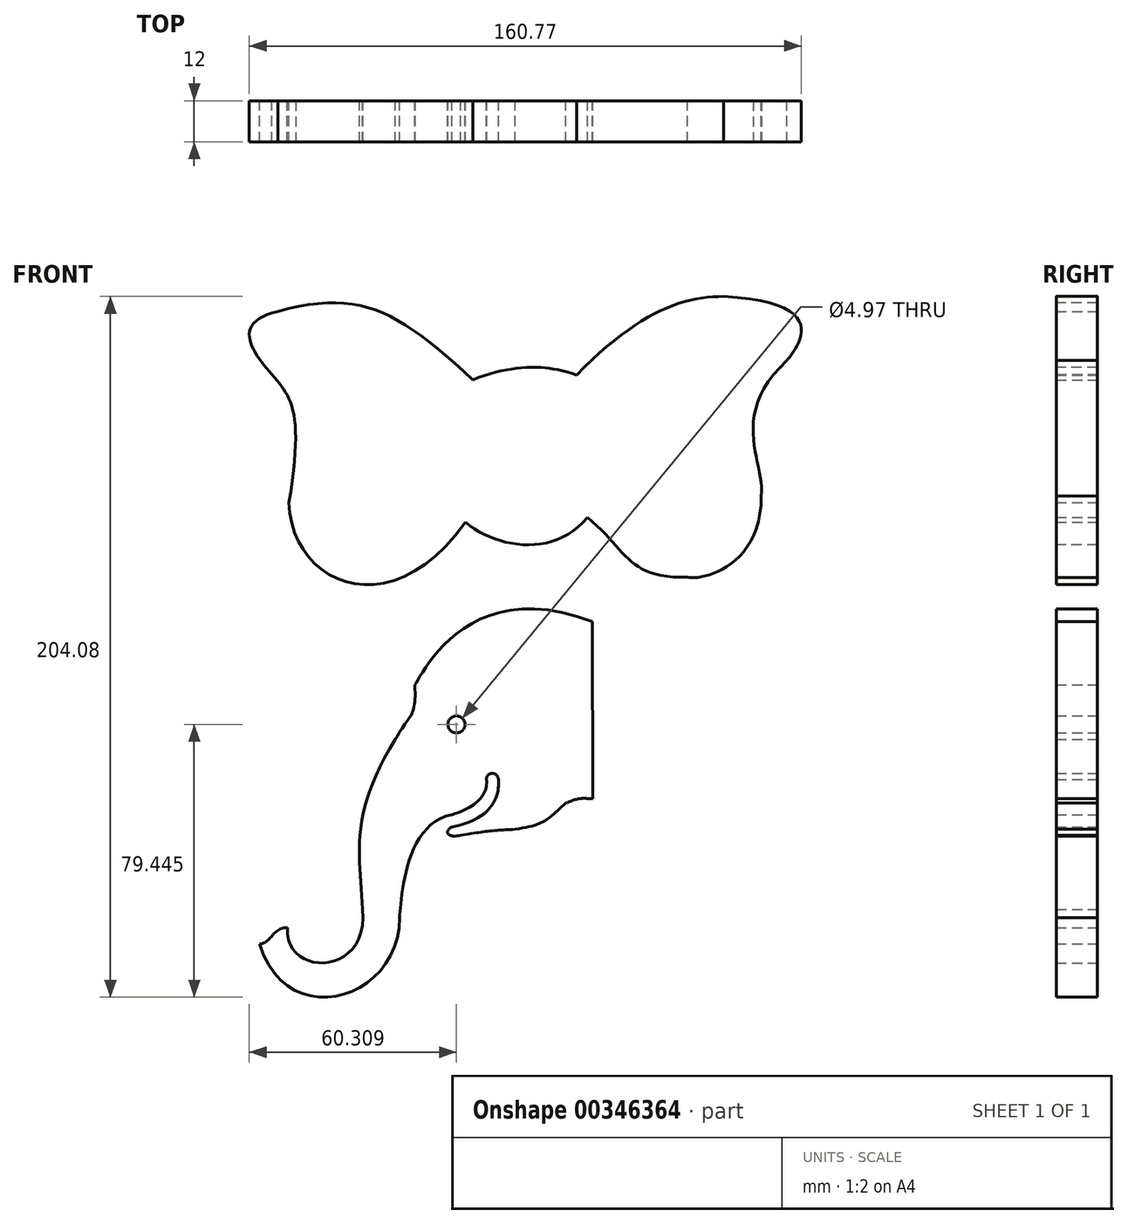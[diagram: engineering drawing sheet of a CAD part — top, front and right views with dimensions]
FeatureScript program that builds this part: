
annotation { "Feature Type Name" : "Feature", "Feature Type Description" : "" }
export const myFeature = defineFeature(function(context is Context, id is Id, definition is map)
    precondition{}
    {
        {
            var Q0;
            Q0=qCreatedBy(makeId("Front.planeOp"),FACE);
            var sketch = newSketch(context, id + "F0", { "sketchPlane" : qUnion([Q0])});
            skFitSpline(sketch, "E0", {"points": [v(-71.13, -54.1) * mm, v(-41, -52.71) * mm], "startDerivative": vector(38.1, 16.38) * mm, "endDerivative": vector(16.93, -7.18) * mm});
            skFitSpline(sketch, "E1", {"points": [v(-41, -52.71) * mm, v(1.84, -29.82) * mm], "startDerivative": vector(52.97, 54.2) * mm, "endDerivative": vector(35.72, -0.65) * mm});
            skFitSpline(sketch, "E2", {"points": [v(1.84, -29.82) * mm, v(20.3, -48.4) * mm], "startDerivative": vector(99.15, -5.13) * mm, "endDerivative": vector(-7.47, -9.38) * mm});
            skFitSpline(sketch, "E3", {"points": [v(20.3, -48.4) * mm, v(12.8, -87.94) * mm], "startDerivative": vector(-52.35, -49.57) * mm, "endDerivative": vector(-3.9, -29.42) * mm});
            skFitSpline(sketch, "E4", {"points": [v(12.8, -87.94) * mm, v(-8.74, -111.56) * mm], "startDerivative": vector(0.04, -63.12) * mm, "endDerivative": vector(-11.14, 3.4) * mm});
            skFitSpline(sketch, "E5", {"points": [v(-8.74, -111.56) * mm, v(-37.79, -94.18) * mm], "startDerivative": vector(-52.12, -1.48) * mm, "endDerivative": vector(-35.02, 28.89) * mm});
            skFitSpline(sketch, "E6", {"points": [v(-37.79, -94.18) * mm, v(-73.34, -95.58) * mm], "startDerivative": vector(-29.85, -35.3) * mm, "endDerivative": vector(-28.23, 22.76) * mm});
            skFitSpline(sketch, "E7", {"points": [v(-73.34, -95.58) * mm, v(-124.72, -89.87) * mm], "startDerivative": vector(-65.32, -92.34) * mm, "endDerivative": vector(-2.2, 71.35) * mm});
            skFitSpline(sketch, "E8", {"points": [v(-124.72, -89.87) * mm, v(-129.7, -52.53) * mm], "startDerivative": vector(13.03, 80.56) * mm, "endDerivative": vector(-17.29, 20.24) * mm});
            skFitSpline(sketch, "E9", {"points": [v(-129.7, -52.53) * mm, v(-127.98, -34.17) * mm], "startDerivative": vector(-17.83, 20.3) * mm, "endDerivative": vector(40.92, 9.85) * mm});
            skFitSpline(sketch, "E10", {"points": [v(-127.98, -34.17) * mm, v(-71.13, -54.1) * mm], "startDerivative": vector(73.6, 20.36) * mm, "endDerivative": vector(65.04, -59.48) * mm});
            skFitSpline(sketch, "E11", {"points": [v(-36.4, -124.53) * mm, v(-88.08, -142.94) * mm], "startDerivative": vector(-108.22, 41.82) * mm, "endDerivative": vector(-6.83, -9.83) * mm});
            skFitSpline(sketch, "E12", {"points": [v(-88.08, -142.94) * mm, v(-93.73, -158.82) * mm], "startDerivative": vector(1.9, -28.6) * mm, "endDerivative": vector(-12.28, -22.44) * mm});
            skFitSpline(sketch, "E13", {"points": [v(-93.73, -158.82) * mm, v(-103.28, -208.3) * mm], "startDerivative": vector(-41.07, -65) * mm, "endDerivative": vector(2.58, -47.23) * mm});
            skFitSpline(sketch, "E14", {"points": [v(-103.28, -208.3) * mm, v(-125.21, -213.68) * mm], "startDerivative": vector(6, -59.92) * mm, "endDerivative": vector(2.79, 42.84) * mm});
            skFitSpline(sketch, "E15", {"points": [v(-125.21, -213.68) * mm, v(-133.24, -218.42) * mm], "startDerivative": vector(-11.6, 1.1) * mm, "endDerivative": vector(-9.63, -0.66) * mm});
            skFitSpline(sketch, "E16", {"points": [v(-133.24, -218.42) * mm, v(-92.53, -210.69) * mm], "startDerivative": vector(23.53, -78.25) * mm, "endDerivative": vector(-0.46, 72.05) * mm});
            skFitSpline(sketch, "E17", {"points": [v(-92.53, -210.69) * mm, v(-77.3, -180.75) * mm], "startDerivative": vector(1.82, 14.96) * mm, "endDerivative": vector(42.14, 8.1) * mm});
            skFitSpline(sketch, "E18", {"points": [v(-74.7, -186.74) * mm, v(-58.9, -185.01) * mm], "startDerivative": vector(18.59, 3.23) * mm, "endDerivative": vector(16.16, 0.5) * mm});
            skFitSpline(sketch, "E19", {"points": [v(-58.9, -185.01) * mm, v(-44.1, -177.38) * mm], "startDerivative": vector(28.48, 4.32) * mm, "endDerivative": vector(16.75, 14.17) * mm});
            skFitSpline(sketch, "E20", {"points": [v(-44.1, -177.38) * mm, v(-36.23, -176.08) * mm], "startDerivative": vector(12.9, 5.44) * mm, "endDerivative": vector(9.56, -0.2) * mm});
            skLineSegment(sketch, "E21", {"start": v(-36.4, -124.53) * mm, "end": v(-36.23, -176.08) * mm});
            skCircle(sketch, "E22", {"center": v(-75.95, -154.45) * mm, "radius": 2.48 * mm});
            skFitSpline(sketch, "E23", {"points": [v(-77.3, -180.75) * mm, v(-67.2, -170.5) * mm], "startDerivative": vector(23.23, 7.03) * mm, "endDerivative": vector(-1.48, 11.95) * mm});
            skFitSpline(sketch, "E24", {"points": [v(-67.2, -170.5) * mm, v(-63.72, -170.47) * mm], "startDerivative": vector(-0.27, 7.09) * mm, "endDerivative": vector(0.48, -7.24) * mm});
            skFitSpline(sketch, "E25", {"points": [v(-63.72, -170.47) * mm, v(-77.26, -184.31) * mm], "startDerivative": vector(0.38, -4.05) * mm, "endDerivative": vector(-43.63, -8.02) * mm});
            skFitSpline(sketch, "E26", {"points": [v(-77.26, -184.31) * mm, v(-74.7, -186.74) * mm], "startDerivative": vector(-6.63, -3.47) * mm, "endDerivative": vector(12.81, 2.73) * mm});
            skSolve(sketch);
        }
        {
            var Q0;
            Q0=makeQuery(id+"F0.imprint","IMPRINT",FACE,{"disambiguationData":[TD([[makeQuery(id+"F0.imprint","IMPRINT",EDGE,{"derivedFrom":sQuery(id+"F0.wireOp",EDGE,"E0")}),-1.0]])]});
            var Q1;
            Q1=makeQuery(id+"F0.imprint","IMPRINT",FACE,{"disambiguationData":[TD([[makeQuery(id+"F0.imprint","IMPRINT",EDGE,{"derivedFrom":sQuery(id+"F0.wireOp",EDGE,"E11")}),1.0]])]});
            extrude(context, id + "F1", {"entities" : qUnion([Q0, Q1]), "depth" : 12 * mm});
        }
    });
